# Revit family: flat_polymero_311943_002_4_19_54c4
name_source: partatom
category: Lighting Fixtures
units: mm (PartAtom-declared; Revit-internal decimal feet)

## family parameters
Cut with Voids When Loaded = No
Host = Face
Light Source = No
Part Type = Normal
Room Calculation Point = No
Round Connector Dimension = Use Diameter
Shared = No

## types (1)
- FLAT POLYMERO (1 x LED Modul 840, 1200 lm, 4000)
    Apparent Load = 12 VA
    CIE Flux Codes = 41 70 89 86 100
    Color Rendering = 80
    Color Temperature = 4000
    Default Elevation = 1800 mm
    Description = Series: FLAT POLYMERO
Decorative round surface-mounted luminaire. Base: metal, powder-coated. Diffuser made of plastic (polycarbonate), opal, shockproof. Diffuser fastening: patented push system. Suitable for Ceiling mounting, Wall (surface). With integrated HF movement sensor. Functional parameters of a master luminaire (ceiling height of approx. 2.8 m): HF detector 24 GHz with integrated corridor function. Coverage: approx. 130° radial. Easy adjustment of functions via 3 associated push button switches. Sensitivity/Range: 0.5-5 m radial, adjustable from 10-100%. Time control 1 second to 15 minutes in 8 different levels. Daylight detection with 5 brightness levels and learning mode. Up to 9 slave luminaires can be operated with one master luminaire (max. up to 150 W / 230 W). Suitable for outdoor use to a limited extent only, as it is sensitive to all movements. 
Colour: white
Diameter: 300 mm
Height: 100 mm
Lamp: LED exchangeable
Socket: without socket
Colour temperature: 4000K
Colour rendering index (CRI): 83
System power: 12 W
Rated luminous flux: 1200 lm
Beam angle Down: 118°
Luminous efficiency: 100 lm/W
Control gear: Converter not necessary
Protection class: I
Type of protection: IP 40
    Height = 100 mm  [stored 0.328084 ft]
    Lamp = 1 x LED Modul 840
    Lamp Light Flux = 1200 lm
    Lamp count = 1
    Length = 300 mm
    Lifetime = 50000 h
    Luminous efficacy = 100 lm/W
    Manufacturer = RZB
    ModVariant = No
    Model = 311943.002.4.19
    Mounting Place = Ceiling, Wall
    Mounting Type = Surface mounted
    Number of Poles = 1
    OnlyDefault = Yes
    Power Factor = 1
    Product Name = FLAT POLYMERO
    Product group = Surface mounted ceiling and wall luminaires
    ProductGroupID = 305
    Protection Class = Protection class I
    Protection Degree = IP 40
    RLX_Detail_Level = 1
    RLX_Emergency_Light_Flux = 0 lm
    RLX_Emergency_Type = 0
    RLX_Emergency_Type_DB = No
    RlxData = <blob elided: 80145 chars, md5=278abecb>
    Socket = socket
    Standby Power = 0 W
    System Light Flux = 1200 lm
    System Power = 12 W
    Type Comments = ALEA SPOT
    Type Image = 311627.002.5.jpg
    URL = http://relux.com
    VarID = ---
    Voltage = 230 V
    Voltage Range = 220-240 V
    Weight = 0.00 kg
    Width = 0 mm  [stored 0 ft]

note: [stored X ft] marks values corroborated as IEEE doubles in the binary element streams (Revit-internal decimal feet)

## geometry (parser evidence)
native form markers: Sweep x11
no freeform markers — native parametric forms only
